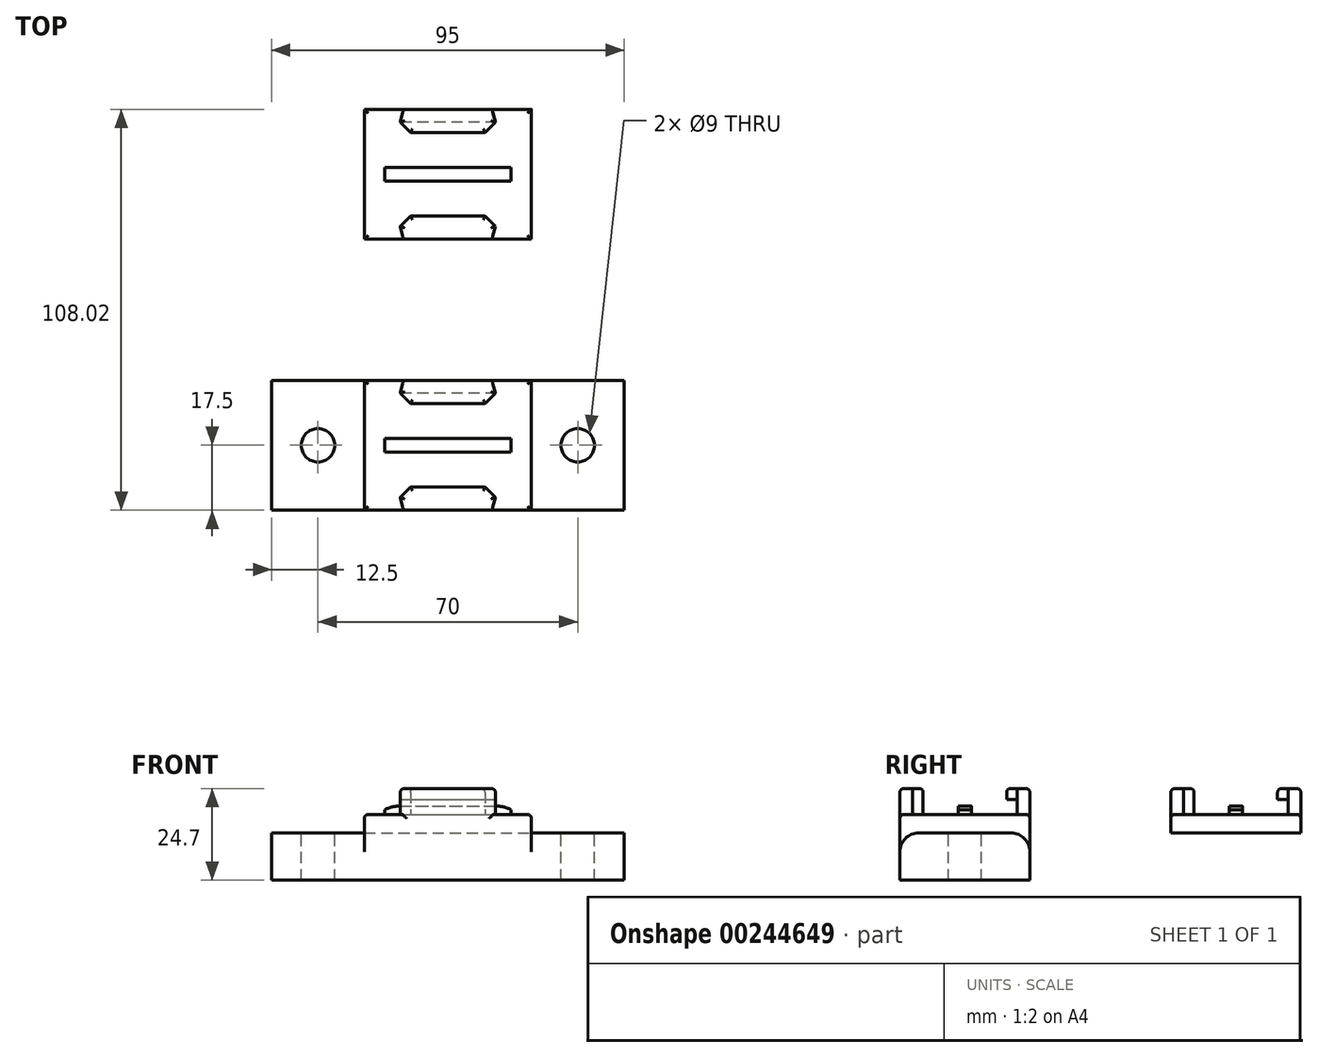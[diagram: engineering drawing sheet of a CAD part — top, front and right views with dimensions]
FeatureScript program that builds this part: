
annotation { "Feature Type Name" : "Feature", "Feature Type Description" : "" }
export const myFeature = defineFeature(function(context is Context, id is Id, definition is map)
    precondition{}
    {
        {
            var Q0;
            Q0=qCreatedBy(makeId("Top.planeOp"),FACE);
            var sketch = newSketch(context, id + "F0", { "sketchPlane" : qUnion([Q0])});
            skLineSegment(sketch, "E0.rect.bottom", {"start": v(-22.5, 17.5) * mm, "end": v(22.5, 17.5) * mm});
            skLineSegment(sketch, "E0.rect.top", {"start": v(-22.5, -17.5) * mm, "end": v(22.5, -17.5) * mm});
            skLineSegment(sketch, "E0.rect.left", {"start": v(-22.5, 17.5) * mm, "end": v(-22.5, -17.5) * mm});
            skLineSegment(sketch, "E0.rect.right", {"start": v(22.5, 17.5) * mm, "end": v(22.5, -17.5) * mm});
            skPoint(sketch, "E0.rect.middle", {"position": v(0, 0) * mm});
            skSolve(sketch);
        }
        {
            var Q0;
            Q0=makeQuery(id+"F0.imprint","IMPRINT",FACE,{"disambiguationData":[TD([[makeQuery(id+"F0.imprint","IMPRINT",EDGE,{"derivedFrom":sQuery(id+"F0.wireOp",EDGE,"E0.rect.bottom")}),-1.0]])]});
            extrude(context, id + "F1", {"entities" : qUnion([Q0]), "depth" : 5 * mm});
        }
        {
            var Q0;
            Q0=makeQuery(id+"F1.opExtrude","CAP_FACE",FACE,{"disambiguationData":[OSD([sQuery(id+"F0.wireOp",EDGE,"E0.rect.bottom"),sQuery(id+"F0.wireOp",EDGE,"E0.rect.top"),sQuery(id+"F0.wireOp",EDGE,"E0.rect.left"),sQuery(id+"F0.wireOp",EDGE,"E0.rect.right")])],"isStart":false});
            var sketch = newSketch(context, id + "F2", { "sketchPlane" : qUnion([Q0])});
            skLineSegment(sketch, "E1.rect.bottom", {"start": v(-17, 1.82) * mm, "end": v(17, 1.82) * mm});
            skLineSegment(sketch, "E1.rect.top", {"start": v(-17, -1.83) * mm, "end": v(17, -1.83) * mm});
            skLineSegment(sketch, "E1.rect.left", {"start": v(-17, 1.82) * mm, "end": v(-17, -1.83) * mm});
            skLineSegment(sketch, "E1.rect.right", {"start": v(17, 1.82) * mm, "end": v(17, -1.83) * mm});
            skPoint(sketch, "E1.rect.middle", {"position": v(0, 0) * mm});
            skSolve(sketch);
        }
        {
            var Q0;
            Q0=makeQuery(id+"F2.imprint","IMPRINT",FACE,{"disambiguationData":[TD([[makeQuery(id+"F2.imprint","IMPRINT",EDGE,{"derivedFrom":sQuery(id+"F2.wireOp",EDGE,"E1.rect.bottom")}),-1.0]])]});
            extrude(context, id + "F3", {"entities" : qUnion([Q0]), "operationType" : NewBodyOperationType.ADD, "depth" : 2.25 * mm});
        }
        {
            var Q0;
            Q0=makeQuery(id+"F3.opExtrude","SWEPT_FACE",FACE,{"disambiguationData":[OSD([sQuery(id+"F2.wireOp",EDGE,"E1.rect.top")])]});
            var sketch = newSketch(context, id + "F4", { "sketchPlane" : qUnion([Q0])});
            skLineSegment(sketch, "E2", {"start": v(-17, 7.25) * mm, "end": v(17, 7.25) * mm, "construction": true});
            skLineSegment(sketch, "E3.0", {"start": v(-17, 6.25) * mm, "end": v(17, 6.25) * mm});
            skArc(sketch, "E4", {"start": v(-13.26, 7.25) * mm, "mid": v(-15.2, 7) * mm, "end": v(-17, 6.25) * mm});
            skLineSegment(sketch, "E5", {"start": v(0, 0) * mm, "end": v(0, 15.47) * mm, "construction": true});
            skArc(sketch, "E6.0.MirrorCS", {"start": v(13.26, 7.25) * mm, "mid": v(15.2, 7) * mm, "end": v(17, 6.25) * mm});
            skLineSegment(sketch, "E7", {"start": v(-17, 6.25) * mm, "end": v(-18.16, 6.25) * mm});
            skLineSegment(sketch, "E8", {"start": v(-18.16, 6.25) * mm, "end": v(-18.16, 8.7) * mm});
            skLineSegment(sketch, "E9", {"start": v(-18.16, 8.7) * mm, "end": v(-13.25, 8.7) * mm});
            skLineSegment(sketch, "E10", {"start": v(-13.25, 8.7) * mm, "end": v(-13.26, 7.25) * mm});
            skLineSegment(sketch, "E11", {"start": v(13.26, 7.25) * mm, "end": v(13.26, 8.4) * mm});
            skLineSegment(sketch, "E12", {"start": v(13.26, 8.4) * mm, "end": v(18.11, 8.4) * mm});
            skLineSegment(sketch, "E13", {"start": v(18.11, 8.4) * mm, "end": v(18.11, 6.28) * mm});
            skLineSegment(sketch, "E14", {"start": v(18.11, 6.28) * mm, "end": v(17, 6.25) * mm});
            skSolve(sketch);
        }
        {
            var Q0;
            {var subQ0=sQuery(id+"F2.wireOp",EDGE,"E1.rect.top");var subQ1=makeQuery(id+"F3.opExtrude","CAP_EDGE",EDGE,{"disambiguationData":[OSD([subQ0])],"isStart":false});var subQ2=sQuery(id+"F4.wireOp",EDGE,"E4");var subQ3=makeQuery(id+"F4.imprint","INTERSECT",VERTEX,{"derivedFrom":[subQ1,subQ2]});var subQ6=makeQuery(id+"F4.imprint","IMPRINT",EDGE,{"disambiguationData":[TD([[subQ3,1.0]])],"derivedFrom":subQ1});var subQ8=sQuery(id+"F4.wireOp",EDGE,"E7");var subQ13=sQuery(id+"F4.wireOp",EDGE,"E6.0.MirrorCS");var subQ18=makeQuery(id+"F4.imprint","INTERSECT",VERTEX,{"derivedFrom":[subQ1,subQ13]});var subQ19=makeQuery(id+"F4.imprint","IMPRINT",EDGE,{"disambiguationData":[TD([[subQ18,-1.0]])],"derivedFrom":subQ1});var subQ20=sQuery(id+"F4.wireOp",EDGE,"E11");Q0=qUnion([makeQuery(id+"F4.imprint","IMPRINT",FACE,{"disambiguationData":[TD([[makeQuery(id+"F4.imprint","IMPRINT",EDGE,{"derivedFrom":subQ8}),-1.0]])]}),makeQuery(id+"F4.imprint","IMPRINT",FACE,{"disambiguationData":[TD([[subQ6,-1.0]])]}),makeQuery(id+"F4.imprint","IMPRINT",FACE,{"disambiguationData":[TD([[makeQuery(id+"F4.imprint","IMPRINT",EDGE,{"derivedFrom":subQ20}),-1.0]])]}),makeQuery(id+"F4.imprint","IMPRINT",FACE,{"disambiguationData":[TD([[subQ19,-1.0]])]})]);}
            extrude(context, id + "F5", {"entities" : qUnion([Q0]), "operationType" : NewBodyOperationType.REMOVE, "endBound" : BoundingType.THROUGH_ALL, "oppositeDirection" : true, "depth" : 25 * mm});
        }
        {
            var Q0;
            Q0=makeQuery(id+"F1.opExtrude","CAP_FACE",FACE,{"disambiguationData":[OSD([sQuery(id+"F0.wireOp",EDGE,"E0.rect.bottom"),sQuery(id+"F0.wireOp",EDGE,"E0.rect.top"),sQuery(id+"F0.wireOp",EDGE,"E0.rect.left"),sQuery(id+"F0.wireOp",EDGE,"E0.rect.right")])],"isStart":false});
            var sketch = newSketch(context, id + "F6", { "sketchPlane" : qUnion([Q0])});
            skLineSegment(sketch, "E15.rect.bottom", {"start": v(-11.94, 17.5) * mm, "end": v(11.94, 17.5) * mm, "construction": true});
            skPoint(sketch, "E15.rect.middle", {"position": v(0, 0) * mm});
            skLineSegment(sketch, "E16.0", {"start": v(-10, 11.25) * mm, "end": v(10, 11.25) * mm});
            skLineSegment(sketch, "E17", {"start": v(-10, 11.25) * mm, "end": v(-12.82, 14.08) * mm, "construction": true});
            skLineSegment(sketch, "E18.0.MirrorCS", {"start": v(10, 11.25) * mm, "end": v(12.82, 14.08) * mm, "construction": true});
            skLineSegment(sketch, "E19", {"start": v(10, 11.25) * mm, "end": v(12.82, 14.08) * mm});
            skLineSegment(sketch, "E20", {"start": v(11.94, 17.5) * mm, "end": v(-11.94, 17.5) * mm});
            skLineSegment(sketch, "E21", {"start": v(-12.82, 14.08) * mm, "end": v(-10, 11.25) * mm});
            skLineSegment(sketch, "E22.0.MirrorCS", {"start": v(-10, -11.25) * mm, "end": v(-12.82, -14.08) * mm, "construction": true});
            skLineSegment(sketch, "E22.1.MirrorCS", {"start": v(-11.94, -17.5) * mm, "end": v(11.94, -17.5) * mm, "construction": true});
            skLineSegment(sketch, "E22.2.MirrorCS", {"start": v(-11.94, -17.5) * mm, "end": v(11.94, -17.5) * mm, "construction": true});
            skLineSegment(sketch, "E22.4.MirrorCS", {"start": v(-10, -11.25) * mm, "end": v(-12.82, -14.08) * mm, "construction": true});
            skLineSegment(sketch, "E22.5.MirrorCS", {"start": v(10, -11.25) * mm, "end": v(12.82, -14.08) * mm, "construction": true});
            skLineSegment(sketch, "E22.7.MirrorCS", {"start": v(11.94, -17.5) * mm, "end": v(-11.94, -17.5) * mm});
            skLineSegment(sketch, "E22.9.MirrorCS", {"start": v(10, -11.25) * mm, "end": v(12.82, -14.08) * mm});
            skLineSegment(sketch, "E22.10.MirrorCS", {"start": v(-12.82, -14.08) * mm, "end": v(-10, -11.25) * mm});
            skLineSegment(sketch, "E22.12.MirrorCS", {"start": v(-10, -11.25) * mm, "end": v(10, -11.25) * mm});
            skLineSegment(sketch, "E23", {"start": v(12.82, 14.08) * mm, "end": v(11.94, 17.5) * mm});
            skLineSegment(sketch, "E24.0.MirrorCS", {"start": v(12.82, -14.08) * mm, "end": v(11.94, -17.5) * mm});
            skLineSegment(sketch, "E25.0.MirrorCS", {"start": v(-12.82, 14.08) * mm, "end": v(-11.94, 17.5) * mm});
            skLineSegment(sketch, "E26.0.MirrorCS", {"start": v(-12.82, -14.08) * mm, "end": v(-11.94, -17.5) * mm});
            skSolve(sketch);
        }
        {
            var Q0;
            {Q0=qUnion([makeQuery(id+"F6.imprint","IMPRINT",FACE,{"disambiguationData":[TD([[makeQuery(id+"F6.imprint","IMPRINT",EDGE,{"derivedFrom":sQuery(id+"F6.wireOp",EDGE,"E16.0")}),1.0]])]}),makeQuery(id+"F6.imprint","IMPRINT",FACE,{"disambiguationData":[TD([[makeQuery(id+"F6.imprint","IMPRINT",EDGE,{"derivedFrom":sQuery(id+"F6.wireOp",EDGE,"E22.7.MirrorCS")}),1.0]])]})]);}
            extrude(context, id + "F7", {"entities" : qUnion([Q0]), "operationType" : NewBodyOperationType.ADD, "depth" : 7 * mm});
        }
        {
            var Q0;
            Q0=qCreatedBy(makeId("Right.planeOp"),FACE);
            var sketch = newSketch(context, id + "F8", { "sketchPlane" : qUnion([Q0])});
            skLineSegment(sketch, "E27.0", {"start": v(14.1, 9) * mm, "end": v(14.1, 5) * mm});
            skLineSegment(sketch, "E28.bottom", {"start": v(14.1, 5) * mm, "end": v(10.15, 5) * mm});
            skLineSegment(sketch, "E28.top", {"start": v(14.1, 9) * mm, "end": v(10.15, 9) * mm});
            skLineSegment(sketch, "E28.left", {"start": v(14.1, 5) * mm, "end": v(14.1, 9) * mm});
            skLineSegment(sketch, "E28.right", {"start": v(10.15, 5) * mm, "end": v(10.15, 9) * mm});
            skLineSegment(sketch, "E29.0.MirrorCS", {"start": v(-14.1, 5) * mm, "end": v(-14.1, 9) * mm});
            skLineSegment(sketch, "E29.1.MirrorCS", {"start": v(-14.1, 9) * mm, "end": v(-14.1, 5) * mm});
            skLineSegment(sketch, "E29.2.MirrorCS", {"start": v(-14.1, 9) * mm, "end": v(-10.15, 9) * mm});
            skLineSegment(sketch, "E29.3.MirrorCS", {"start": v(-10.15, 5) * mm, "end": v(-10.15, 9) * mm});
            skLineSegment(sketch, "E29.4.MirrorCS", {"start": v(-14.1, 5) * mm, "end": v(-10.15, 5) * mm});
            skSolve(sketch);
        }
        {
            var Q0;
            {Q0=qUnion([makeQuery(id+"F8.imprint","IMPRINT",FACE,{"disambiguationData":[TD([[makeQuery(id+"F8.imprint","IMPRINT",EDGE,{"derivedFrom":sQuery(id+"F8.wireOp",EDGE,"E28.bottom")}),-1.0]])]}),makeQuery(id+"F8.imprint","IMPRINT",FACE,{"disambiguationData":[TD([[makeQuery(id+"F8.imprint","IMPRINT",EDGE,{"derivedFrom":sQuery(id+"F8.wireOp",EDGE,"E29.1.MirrorCS")}),1.0]])]})]);}
            extrude(context, id + "F9", {"entities" : qUnion([Q0]), "operationType" : NewBodyOperationType.REMOVE, "endBound" : BoundingType.SYMMETRIC, "oppositeDirection" : true, "depth" : 31.01 * mm});
        }
        {
            var Q0;
            Q0=makeQuery(id+"F7.opExtrude","CAP_FACE",FACE,{"disambiguationData":[OSD([sQuery(id+"F6.wireOp",EDGE,"E16.0"),sQuery(id+"F6.wireOp",EDGE,"E19"),sQuery(id+"F6.wireOp",EDGE,"E20"),sQuery(id+"F6.wireOp",EDGE,"E21"),sQuery(id+"F6.wireOp",EDGE,"E23"),sQuery(id+"F6.wireOp",EDGE,"E25.0.MirrorCS")])],"isStart":false});
            var Q1;
            Q1=makeQuery(id+"F7.opExtrude","CAP_FACE",FACE,{"disambiguationData":[OSD([sQuery(id+"F6.wireOp",EDGE,"E22.7.MirrorCS"),sQuery(id+"F6.wireOp",EDGE,"E22.9.MirrorCS"),sQuery(id+"F6.wireOp",EDGE,"E22.10.MirrorCS"),sQuery(id+"F6.wireOp",EDGE,"E22.12.MirrorCS"),sQuery(id+"F6.wireOp",EDGE,"E24.0.MirrorCS"),sQuery(id+"F6.wireOp",EDGE,"E26.0.MirrorCS")])],"isStart":false});
            var Q2;
            Q2=makeQuery(id+"F7.opExtrude","SWEPT_EDGE",EDGE,{"disambiguationData":[OSD([sQuery(id+"F0.wireOp",EDGE,"E0.rect.bottom"),sQuery(id+"F6.wireOp",EDGE,"E20"),sQuery(id+"F6.wireOp",EDGE,"E23")])]});
            var Q3;
            Q3=makeQuery(id+"F7.opExtrude","SWEPT_EDGE",EDGE,{"disambiguationData":[OSD([sQuery(id+"F0.wireOp",EDGE,"E0.rect.bottom"),sQuery(id+"F6.wireOp",EDGE,"E20"),sQuery(id+"F6.wireOp",EDGE,"E25.0.MirrorCS")])]});
            var Q4;
            Q4=makeQuery(id+"F7.opExtrude","SWEPT_EDGE",EDGE,{"disambiguationData":[OSD([sQuery(id+"F0.wireOp",EDGE,"E0.rect.top"),sQuery(id+"F6.wireOp",EDGE,"E22.7.MirrorCS"),sQuery(id+"F6.wireOp",EDGE,"E24.0.MirrorCS")])]});
            var Q5;
            Q5=makeQuery(id+"F7.opExtrude","SWEPT_EDGE",EDGE,{"disambiguationData":[OSD([sQuery(id+"F0.wireOp",EDGE,"E0.rect.top"),sQuery(id+"F6.wireOp",EDGE,"E22.7.MirrorCS"),sQuery(id+"F6.wireOp",EDGE,"E26.0.MirrorCS")])]});
            fillet(context, id + "F10", {"entities" : qUnion([Q0, Q1, Q2, Q3, Q4, Q5]), "radius" : 1 * mm, "tangentPropagation" : true, "allowEdgeOverflow" : false});
        }
        {
            var Q0;
            {var subQ0=sQuery(id+"F0.wireOp",EDGE,"E0.rect.top");var subQ1=sQuery(id+"F0.wireOp",EDGE,"E0.rect.right");Q0=makeQuery(id+"F7.boolean.opBoolean","SPLIT",EDGE,{"disambiguationData":[TD([makeQuery(id+"F1.opExtrude","SWEPT_FACE",FACE,{"disambiguationData":[OSD([subQ1])]})])],"derivedFrom":makeQuery(id+"F1.opExtrude","CAP_EDGE",EDGE,{"disambiguationData":[OSD([subQ0])],"isStart":false})});}
            var Q1;
            Q1=makeQuery(id+"F1.opExtrude","CAP_EDGE",EDGE,{"disambiguationData":[OSD([sQuery(id+"F0.wireOp",EDGE,"E0.rect.right")])],"isStart":false});
            var Q2;
            {var subQ0=sQuery(id+"F0.wireOp",EDGE,"E0.rect.bottom");var subQ1=sQuery(id+"F0.wireOp",EDGE,"E0.rect.right");Q2=makeQuery(id+"F7.boolean.opBoolean","SPLIT",EDGE,{"disambiguationData":[TD([makeQuery(id+"F1.opExtrude","SWEPT_FACE",FACE,{"disambiguationData":[OSD([subQ1])]})])],"derivedFrom":makeQuery(id+"F1.opExtrude","CAP_EDGE",EDGE,{"disambiguationData":[OSD([subQ0])],"isStart":false})});}
            var Q3;
            {var subQ0=sQuery(id+"F0.wireOp",EDGE,"E0.rect.bottom");var subQ1=sQuery(id+"F0.wireOp",EDGE,"E0.rect.left");Q3=makeQuery(id+"F7.boolean.opBoolean","SPLIT",EDGE,{"disambiguationData":[TD([makeQuery(id+"F1.opExtrude","SWEPT_FACE",FACE,{"disambiguationData":[OSD([subQ1])]})])],"derivedFrom":makeQuery(id+"F1.opExtrude","CAP_EDGE",EDGE,{"disambiguationData":[OSD([subQ0])],"isStart":false})});}
            var Q4;
            Q4=makeQuery(id+"F1.opExtrude","CAP_EDGE",EDGE,{"disambiguationData":[OSD([sQuery(id+"F0.wireOp",EDGE,"E0.rect.left")])],"isStart":false});
            var Q5;
            {var subQ0=sQuery(id+"F0.wireOp",EDGE,"E0.rect.top");var subQ1=sQuery(id+"F0.wireOp",EDGE,"E0.rect.left");Q5=makeQuery(id+"F7.boolean.opBoolean","SPLIT",EDGE,{"disambiguationData":[TD([makeQuery(id+"F1.opExtrude","SWEPT_FACE",FACE,{"disambiguationData":[OSD([subQ1])]})])],"derivedFrom":makeQuery(id+"F1.opExtrude","CAP_EDGE",EDGE,{"disambiguationData":[OSD([subQ0])],"isStart":false})});}
            fillet(context, id + "F11", {"entities" : qUnion([Q0, Q1, Q2, Q3, Q4, Q5]), "radius" : 1 * mm, "allowEdgeOverflow" : false});
        }
        {
            var Q0;
            Q0=makeQuery(id+"F1.opExtrude","SWEPT_BODY",BODY,{"disambiguationData":[OSD([sQuery(id+"F0.wireOp",EDGE,"E0.rect.bottom"),sQuery(id+"F0.wireOp",EDGE,"E0.rect.top"),sQuery(id+"F0.wireOp",EDGE,"E0.rect.left"),sQuery(id+"F0.wireOp",EDGE,"E0.rect.right")])]});
            transform(context, id + "F12", {"entities" : qUnion([Q0]), "transformType" : TransformType.TRANSLATION_3D, "dx" : 0 * mm, "dy" : 73.02 * mm, "dz" : 0 * mm, "makeCopy" : true});
        }
        {
            var Q0;
            Q0=makeQuery(id+"F0.imprint","IMPRINT",FACE,{"disambiguationData":[TD([[makeQuery(id+"F0.imprint","IMPRINT",EDGE,{"derivedFrom":sQuery(id+"F0.wireOp",EDGE,"E0.rect.bottom")}),-1.0]])]});
            extrude(context, id + "F13", {"entities" : qUnion([Q0]), "operationType" : NewBodyOperationType.ADD, "oppositeDirection" : true, "depth" : 12.7 * mm});
        }
        {
            var Q0;
            {var subQ0=sQuery(id+"F0.wireOp",EDGE,"E0.rect.left");Q0=makeQuery(id+"F13.boolean.opBoolean","MERGE",FACE,{"derivedFrom":[makeQuery(id+"F1.opExtrude","SWEPT_FACE",FACE,{"disambiguationData":[OSD([subQ0])]}),makeQuery(id+"F13.opExtrude","SWEPT_FACE",FACE,{"disambiguationData":[OSD([subQ0])]})]});}
            var sketch = newSketch(context, id + "F14", { "sketchPlane" : qUnion([Q0])});
            skLineSegment(sketch, "E30.bottom", {"start": v(-17.5, -12.7) * mm, "end": v(17.5, -12.7) * mm});
            skLineSegment(sketch, "E30.top", {"start": v(-17.5, 0) * mm, "end": v(17.5, 0) * mm});
            skLineSegment(sketch, "E30.left", {"start": v(-17.5, -12.7) * mm, "end": v(-17.5, 0) * mm});
            skLineSegment(sketch, "E30.right", {"start": v(17.5, -12.7) * mm, "end": v(17.5, 0) * mm});
            skSolve(sketch);
        }
        {
            var Q0;
            {var subQ0=sQuery(id+"F0.wireOp",EDGE,"E0.rect.right");Q0=makeQuery(id+"F13.boolean.opBoolean","MERGE",FACE,{"derivedFrom":[makeQuery(id+"F1.opExtrude","SWEPT_FACE",FACE,{"disambiguationData":[OSD([subQ0])]}),makeQuery(id+"F13.opExtrude","SWEPT_FACE",FACE,{"disambiguationData":[OSD([subQ0])]})]});}
            var sketch = newSketch(context, id + "F15", { "sketchPlane" : qUnion([Q0])});
            skLineSegment(sketch, "E31.bottom", {"start": v(-17.5, -12.7) * mm, "end": v(17.5, -12.7) * mm});
            skLineSegment(sketch, "E31.top", {"start": v(-17.5, 0) * mm, "end": v(17.5, 0) * mm});
            skLineSegment(sketch, "E31.left", {"start": v(-17.5, -12.7) * mm, "end": v(-17.5, 0) * mm});
            skLineSegment(sketch, "E31.right", {"start": v(17.5, -12.7) * mm, "end": v(17.5, 0) * mm});
            skSolve(sketch);
        }
        {
            var Q0;
            Q0=makeQuery(id+"F14.imprint","IMPRINT",FACE,{"disambiguationData":[TD([[makeQuery(id+"F14.imprint","IMPRINT",EDGE,{"derivedFrom":sQuery(id+"F14.wireOp",EDGE,"E30.bottom")}),1.0]])]});
            extrude(context, id + "F16", {"entities" : qUnion([Q0]), "operationType" : NewBodyOperationType.ADD, "depth" : 25 * mm});
        }
        {
            var Q0;
            Q0=makeQuery(id+"F16.opExtrude","SWEPT_EDGE",EDGE,{"disambiguationData":[OSD([sQuery(id+"F0.wireOp",EDGE,"E0.rect.top"),sQuery(id+"F0.wireOp",EDGE,"E0.rect.left"),sQuery(id+"F14.wireOp",EDGE,"E30.top"),sQuery(id+"F14.wireOp",EDGE,"E30.right")])]});
            var Q1;
            Q1=makeQuery(id+"F16.opExtrude","SWEPT_EDGE",EDGE,{"disambiguationData":[OSD([sQuery(id+"F0.wireOp",EDGE,"E0.rect.bottom"),sQuery(id+"F0.wireOp",EDGE,"E0.rect.left"),sQuery(id+"F14.wireOp",EDGE,"E30.top"),sQuery(id+"F14.wireOp",EDGE,"E30.left")])]});
            fillet(context, id + "F17", {"entities" : qUnion([Q0, Q1]), "radius" : 5 * mm, "tangentPropagation" : true, "allowEdgeOverflow" : false});
        }
        {
            var Q0;
            Q0=makeQuery(id+"F15.imprint","IMPRINT",FACE,{"disambiguationData":[TD([[makeQuery(id+"F15.imprint","IMPRINT",EDGE,{"derivedFrom":sQuery(id+"F15.wireOp",EDGE,"E31.bottom")}),-1.0]])]});
            extrude(context, id + "F18", {"entities" : qUnion([Q0]), "operationType" : NewBodyOperationType.ADD, "depth" : 25 * mm});
        }
        {
            var Q0;
            Q0=makeQuery(id+"F18.opExtrude","SWEPT_EDGE",EDGE,{"disambiguationData":[OSD([sQuery(id+"F0.wireOp",EDGE,"E0.rect.top"),sQuery(id+"F0.wireOp",EDGE,"E0.rect.right"),sQuery(id+"F15.wireOp",EDGE,"E31.top"),sQuery(id+"F15.wireOp",EDGE,"E31.left")])]});
            var Q1;
            Q1=makeQuery(id+"F18.opExtrude","SWEPT_EDGE",EDGE,{"disambiguationData":[OSD([sQuery(id+"F0.wireOp",EDGE,"E0.rect.bottom"),sQuery(id+"F0.wireOp",EDGE,"E0.rect.right"),sQuery(id+"F15.wireOp",EDGE,"E31.top"),sQuery(id+"F15.wireOp",EDGE,"E31.right")])]});
            fillet(context, id + "F19", {"entities" : qUnion([Q0, Q1]), "radius" : 5 * mm, "tangentPropagation" : true, "allowEdgeOverflow" : false});
        }
        {
            var Q0;
            Q0=makeQuery(id+"F16.opExtrude","SWEPT_FACE",FACE,{"disambiguationData":[OSD([sQuery(id+"F14.wireOp",EDGE,"E30.top")])]});
            var sketch = newSketch(context, id + "F20", { "sketchPlane" : qUnion([Q0])});
            skCircle(sketch, "E32", {"center": v(-35, 0) * mm, "radius": 4.5 * mm});
            skPoint(sketch, "E32.centerSnap0", {"position": v(-35, 12.5) * mm});
            skSolve(sketch);
        }
        {
            var Q0;
            Q0=makeQuery(id+"F18.opExtrude","SWEPT_FACE",FACE,{"disambiguationData":[OSD([sQuery(id+"F15.wireOp",EDGE,"E31.top")])]});
            var sketch = newSketch(context, id + "F21", { "sketchPlane" : qUnion([Q0])});
            skCircle(sketch, "E33", {"center": v(35, 0) * mm, "radius": 4.5 * mm});
            skPoint(sketch, "E33.centerSnap0", {"position": v(35, 12.5) * mm});
            skSolve(sketch);
        }
        {
            var Q0;
            Q0=makeQuery(id+"F21.imprint","IMPRINT",FACE,{"disambiguationData":[TD([[makeQuery(id+"F21.imprint","IMPRINT",EDGE,{"derivedFrom":sQuery(id+"F21.wireOp",EDGE,"E33")}),1.0]])]});
            extrude(context, id + "F22", {"entities" : qUnion([Q0]), "operationType" : NewBodyOperationType.REMOVE, "oppositeDirection" : true, "depth" : 25 * mm});
        }
        {
            var Q0;
            Q0=makeQuery(id+"F20.imprint","IMPRINT",FACE,{"disambiguationData":[TD([[makeQuery(id+"F20.imprint","IMPRINT",EDGE,{"derivedFrom":sQuery(id+"F20.wireOp",EDGE,"E32")}),1.0]])]});
            extrude(context, id + "F23", {"entities" : qUnion([Q0]), "operationType" : NewBodyOperationType.REMOVE, "oppositeDirection" : true, "depth" : 25 * mm});
        }
    });
